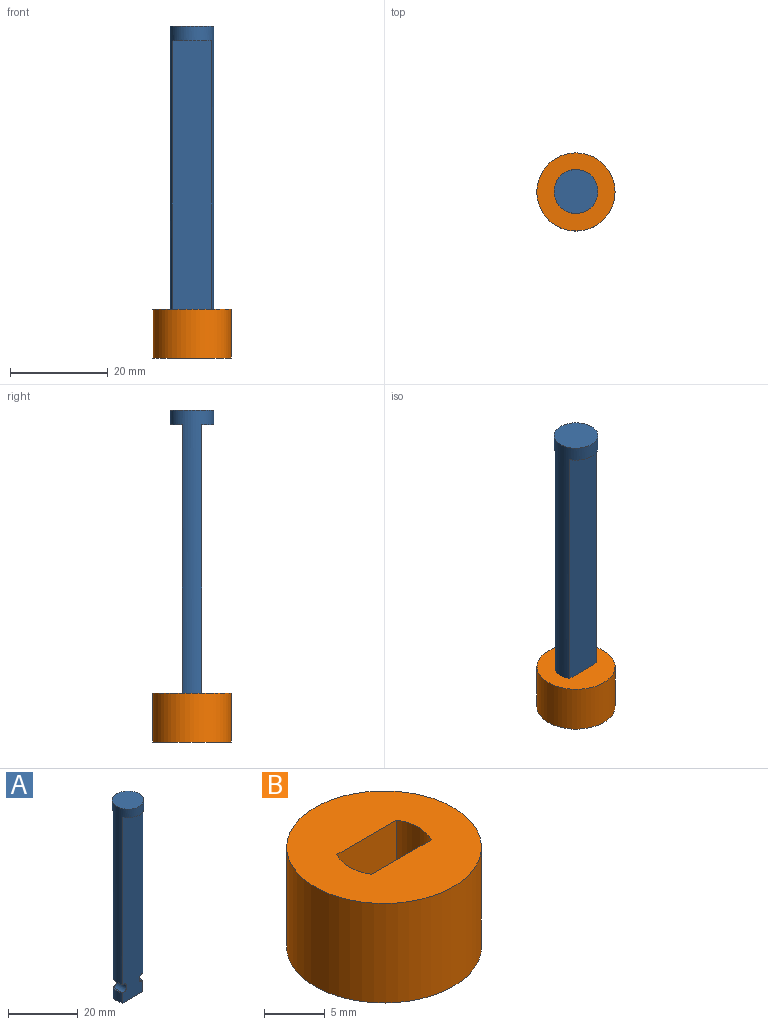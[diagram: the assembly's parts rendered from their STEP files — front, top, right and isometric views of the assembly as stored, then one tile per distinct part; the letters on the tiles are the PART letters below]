
ASSEMBLY  parts=2 mates=1
PART A: 15 faces, bbox 9x9x68 mm
  f0: cylinder r=4.5mm len=4mm, axis (0,0,1), area 14.5mm2, adj f2,f4,f6,f14
  f1: cylinder r=4.5mm len=61.5mm, axis (0,0,1), area 569.8mm2, adj f2,f5,f6,f7,f8,f9,f13
  f2: plane 65x8.06mm, normal (0,-1,0), area 517mm2, adj f0,f1,f3,f4,f8,f10,f12
  f3: cylinder r=4.5mm len=4mm, axis (0,0,1), area 14.5mm2, adj f2,f4,f6,f11
  f4: plane 9x4mm, normal (0,0,-1), area 34.8mm2, adj f0,f2,f3,f6
  f5: plane 9x9mm, normal (0,0,1), area 63.6mm2, adj f1
  f6: plane 65x8.06mm, normal (0,1,0), area 517mm2, adj f0,f1,f3,f4,f7,f10,f12
  f7: plane 8.06x2.5mm, normal (0,0,-1), area 14.4mm2, adj f1,f6
  f8: plane 8.06x2.5mm, normal (0,0,-1), area 14.4mm2, adj f1,f2
  f9: plane 4x0.47mm, normal (0,0,-1), area 1.3mm2, adj f1,f10
  f10: cylinder r=1.5mm len=4mm, axis (0,-1,0), area 18.8mm2, adj f2,f6,f9,f11
  f11: plane 4x0.47mm, normal (0,0,1), area 1.3mm2, adj f3,f10
  f12: cylinder r=1.5mm len=4mm, axis (0,-1,0), area 18.8mm2, adj f2,f6,f13,f14
  f13: plane 4x0.47mm, normal (0,0,-1), area 1.3mm2, adj f1,f12
  f14: plane 4x0.47mm, normal (0,0,1), area 1.3mm2, adj f0,f12
PART B: 7 faces, bbox 16x16x10 mm
  f0: cylinder r=4mm len=10mm, axis (0,0,1), area 41.9mm2, adj f1,f3,f5,f6
  f1: plane 10x6.93mm, normal (0,-1,0), area 69.3mm2, adj f0,f2,f5,f6
  f2: cylinder r=4mm len=10mm, axis (0,0,1), area 41.9mm2, adj f1,f3,f5,f6
  f3: plane 10x6.93mm, normal (0,1,0), area 69.3mm2, adj f0,f2,f5,f6
  f4: cylinder r=8mm len=16mm, axis (0,0,1), area 502.7mm2, adj f5,f6
  f5: plane 16x16mm, normal (0,0,-1), area 170.5mm2, adj f0,f1,f2,f3,f4
  f6: plane 16x16mm, normal (0,0,1), area 170.5mm2, adj f0,f1,f2,f3,f4
PLACE A t=(-44.5,-35.66,37.86)mm
PLACE B t=(-44.5,-35.66,-20.14)mm
MATE revolute A.f0 <-> B.f4  axis (0,0,-1) through (-44.5,-35.66,-30.14)mm
